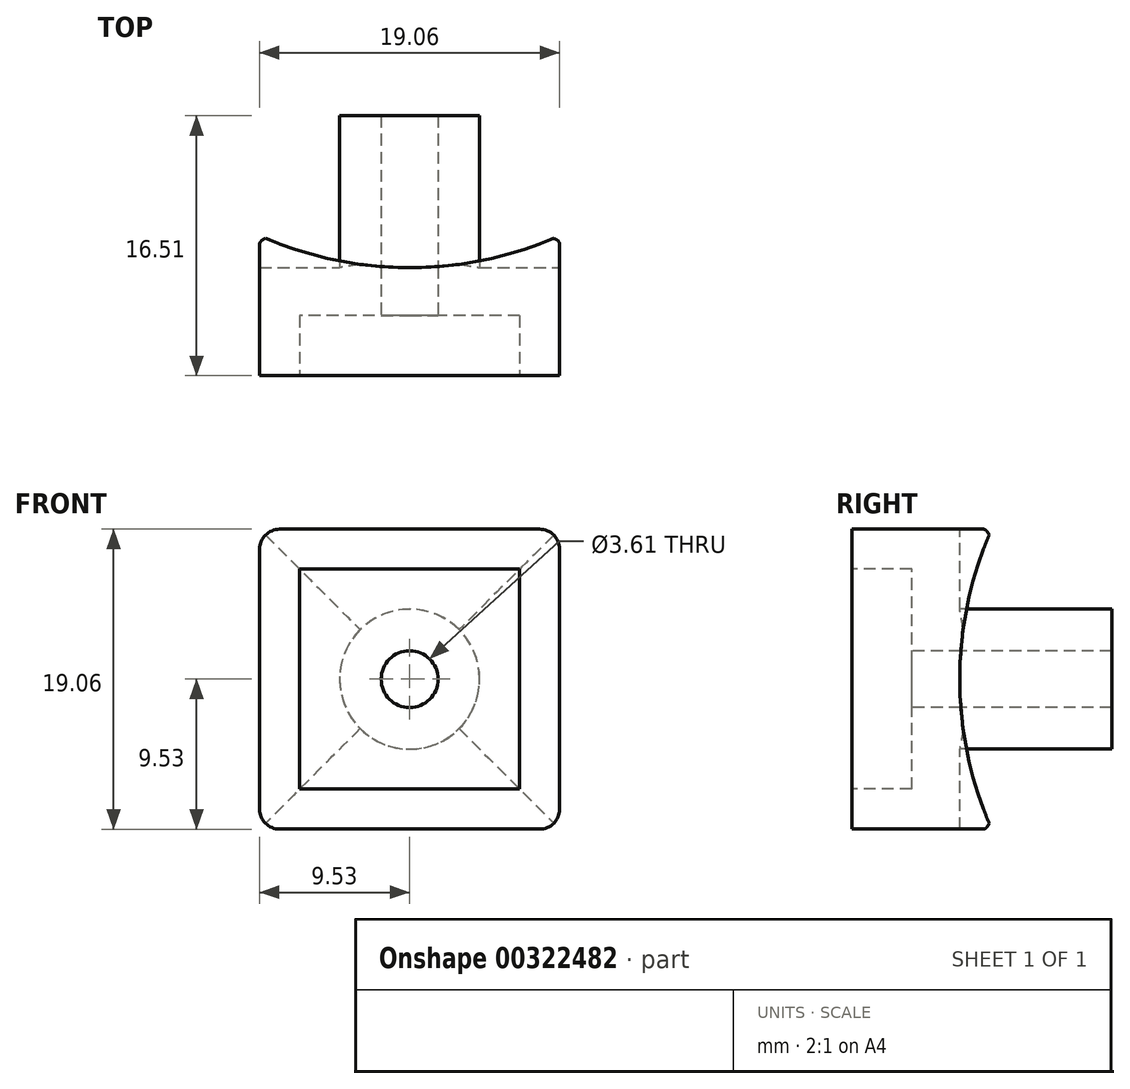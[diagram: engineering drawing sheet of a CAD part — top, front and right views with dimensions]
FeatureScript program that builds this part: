
annotation { "Feature Type Name" : "Feature", "Feature Type Description" : "" }
export const myFeature = defineFeature(function(context is Context, id is Id, definition is map)
    precondition{}
    {
        {
            var Q0;
            Q0=qCreatedBy(makeId("Front.planeOp"),FACE);
            var sketch = newSketch(context, id + "F0", { "sketchPlane" : qUnion([Q0])});
            skLineSegment(sketch, "E0.bottom", {"start": v(-9.52, -9.53) * mm, "end": v(9.53, -9.53) * mm});
            skLineSegment(sketch, "E0.top", {"start": v(-9.53, 9.53) * mm, "end": v(9.52, 9.53) * mm});
            skLineSegment(sketch, "E0.left", {"start": v(-9.52, -9.52) * mm, "end": v(-9.53, 9.52) * mm});
            skLineSegment(sketch, "E0.right", {"start": v(9.53, -9.52) * mm, "end": v(9.52, 9.53) * mm});
            skSolve(sketch);
        }
        {
            var Q0;
            Q0=makeQuery(id+"F0.imprint","IMPRINT",FACE,{"disambiguationData":[TD([[makeQuery(id+"F0.imprint","IMPRINT",EDGE,{"derivedFrom":sQuery(id+"F0.wireOp",EDGE,"E0.bottom")}),1.0]])]});
            extrude(context, id + "F1", {"entities" : qUnion([Q0]), "depth" : 11.43 * mm});
        }
        {
            var Q0;
            Q0=makeQuery(id+"F1.opExtrude","SWEPT_FACE",FACE,{"disambiguationData":[OSD([sQuery(id+"F0.wireOp",EDGE,"E0.right")])]});
            var sketch = newSketch(context, id + "F2", { "sketchPlane" : qUnion([Q0])});
            skArc(sketch, "E1", {"start": v(0, 9.52) * mm, "mid": v(-2.03, 0) * mm, "end": v(0, -9.52) * mm});
            skPoint(sketch, "E1.first.point", {"position": v(0, 9.52) * mm});
            skPoint(sketch, "E1.second.point", {"position": v(-2.03, 0) * mm});
            skPoint(sketch, "E1.third.point", {"position": v(0, -9.53) * mm});
            skLineSegment(sketch, "E2.0", {"start": v(-11.43, 9.52) * mm, "end": v(0, 9.52) * mm});
            skLineSegment(sketch, "E3.0", {"start": v(-11.43, -9.53) * mm, "end": v(0, -9.53) * mm});
            skSolve(sketch);
        }
        {
            var Q0;
            {var subQ1=sQuery(id+"F0.wireOp",EDGE,"E0.right");var subQ2=makeQuery(id+"F1.opExtrude","CAP_EDGE",EDGE,{"disambiguationData":[OSD([subQ1])],"isStart":true});Q0=makeQuery(id+"F2.imprint","IMPRINT",FACE,{"disambiguationData":[TD([[makeQuery(id+"F2.imprint","IMPRINT",EDGE,{"derivedFrom":subQ2}),1.0]])]});}
            extrude(context, id + "F3", {"entities" : qUnion([Q0]), "operationType" : NewBodyOperationType.REMOVE, "endBound" : BoundingType.THROUGH_ALL, "oppositeDirection" : true, "depth" : 25.4 * mm});
        }
        {
            var Q0;
            Q0=makeQuery(id+"F1.opExtrude","SWEPT_FACE",FACE,{"disambiguationData":[OSD([sQuery(id+"F0.wireOp",EDGE,"E0.top")])]});
            var sketch = newSketch(context, id + "F4", { "sketchPlane" : qUnion([Q0])});
            skCircle(sketch, "E4", {"center": v(0, 21.3) * mm, "radius": 23.34 * mm});
            skPoint(sketch, "E4.first.point", {"position": v(-9.53, 0) * mm});
            skPoint(sketch, "E4.second.point", {"position": v(0, -2.03) * mm});
            skPoint(sketch, "E4.third.point", {"position": v(9.52, 0) * mm});
            skSolve(sketch);
        }
        {
            var Q0;
            {var subQ1=sQuery(id+"F0.wireOp",EDGE,"E0.right");var subQ2=sQuery(id+"F0.wireOp",EDGE,"E0.top");var subQ3=makeQuery(id+"F3.boolean.opBoolean","MERGE",EDGE,{"derivedFrom":[makeQuery(id+"F1.opExtrude","CAP_EDGE",EDGE,{"disambiguationData":[OSD([subQ2])],"isStart":true}),makeQuery(id+"F3.opExtrude","SWEPT_EDGE",EDGE,{"disambiguationData":[OSD([subQ2,subQ1,sQuery(id+"F2.wireOp",EDGE,"E1")])]})]});Q0=makeQuery(id+"F4.imprint","IMPRINT",FACE,{"disambiguationData":[TD([[makeQuery(id+"F4.imprint","IMPRINT",EDGE,{"derivedFrom":subQ3}),-1.0]])]});}
            extrude(context, id + "F5", {"entities" : qUnion([Q0]), "operationType" : NewBodyOperationType.REMOVE, "endBound" : BoundingType.THROUGH_ALL, "oppositeDirection" : true, "depth" : 25.4 * mm});
        }
        {
            var Q0;
            Q0=makeQuery(id+"F1.opExtrude","CAP_FACE",FACE,{"disambiguationData":[OSD([sQuery(id+"F0.wireOp",EDGE,"E0.bottom"),sQuery(id+"F0.wireOp",EDGE,"E0.top"),sQuery(id+"F0.wireOp",EDGE,"E0.left"),sQuery(id+"F0.wireOp",EDGE,"E0.right")])],"isStart":false});
            var sketch = newSketch(context, id + "F6", { "sketchPlane" : qUnion([Q0])});
            skCircle(sketch, "E5", {"center": v(0, 0) * mm, "radius": 4.45 * mm});
            skCircle(sketch, "E6", {"center": v(0, 0) * mm, "radius": 1.8 * mm});
            skSolve(sketch);
        }
        {
            var Q0;
            Q0=makeQuery(id+"F6.imprint","IMPRINT",FACE,{"disambiguationData":[TD([[makeQuery(id+"F6.imprint","IMPRINT",EDGE,{"derivedFrom":sQuery(id+"F6.wireOp",EDGE,"E5")}),1.0]])]});
            extrude(context, id + "F7", {"entities" : qUnion([Q0]), "operationType" : NewBodyOperationType.ADD, "oppositeDirection" : true, "depth" : 19.05 * mm});
        }
        {
            var Q0;
            Q0=makeQuery(id+"F6.imprint","IMPRINT",FACE,{"disambiguationData":[TD([[makeQuery(id+"F6.imprint","IMPRINT",EDGE,{"derivedFrom":sQuery(id+"F6.wireOp",EDGE,"E6")}),1.0]])]});
            extrude(context, id + "F8", {"entities" : qUnion([Q0]), "operationType" : NewBodyOperationType.REMOVE, "endBound" : BoundingType.THROUGH_ALL, "oppositeDirection" : true, "depth" : 25.4 * mm});
        }
        {
            var Q0;
            Q0=makeQuery(id+"F1.opExtrude","SWEPT_FACE",FACE,{"disambiguationData":[OSD([sQuery(id+"F0.wireOp",EDGE,"E0.right")])]});
            var sketch = newSketch(context, id + "F9", { "sketchPlane" : qUnion([Q0])});
            skLineSegment(sketch, "E7.bottom", {"start": v(-11.43, -9.53) * mm, "end": v(-8.9, -9.53) * mm});
            skLineSegment(sketch, "E7.top", {"start": v(-11.43, 9.52) * mm, "end": v(-8.9, 9.52) * mm});
            skLineSegment(sketch, "E7.left", {"start": v(-11.43, -9.53) * mm, "end": v(-11.43, 9.52) * mm});
            skLineSegment(sketch, "E7.right", {"start": v(-8.9, -9.53) * mm, "end": v(-8.9, 9.52) * mm});
            skSolve(sketch);
        }
        {
            var Q0;
            Q0=makeQuery(id+"F9.imprint","IMPRINT",FACE,{"disambiguationData":[TD([[makeQuery(id+"F9.imprint","IMPRINT",EDGE,{"derivedFrom":sQuery(id+"F9.wireOp",EDGE,"E7.bottom")}),1.0]])]});
            extrude(context, id + "F10", {"entities" : qUnion([Q0]), "operationType" : NewBodyOperationType.REMOVE, "endBound" : BoundingType.THROUGH_ALL, "oppositeDirection" : true, "depth" : 25.4 * mm});
        }
        {
            var Q0;
            Q0=makeQuery(id+"F6.imprint","IMPRINT",FACE,{"disambiguationData":[TD([[makeQuery(id+"F6.imprint","IMPRINT",EDGE,{"derivedFrom":sQuery(id+"F6.wireOp",EDGE,"E5")}),-1.0]])]});
            var sketch = newSketch(context, id + "F11", { "sketchPlane" : qUnion([Q0])});
            skLineSegment(sketch, "E8.bottom", {"start": v(6.99, -6.98) * mm, "end": v(-6.98, -6.99) * mm});
            skLineSegment(sketch, "E8.top", {"start": v(6.98, 6.98) * mm, "end": v(-6.99, 6.98) * mm});
            skLineSegment(sketch, "E8.left", {"start": v(6.99, -6.98) * mm, "end": v(6.98, 6.98) * mm});
            skLineSegment(sketch, "E8.right", {"start": v(-6.98, -6.99) * mm, "end": v(-6.99, 6.98) * mm});
            skSolve(sketch);
        }
        {
            var Q0;
            Q0=makeQuery(id+"F11.imprint","IMPRINT",FACE,{"disambiguationData":[TD([[makeQuery(id+"F11.imprint","IMPRINT",EDGE,{"derivedFrom":sQuery(id+"F11.wireOp",EDGE,"E8.bottom")}),-1.0]])]});
            var Q1;
            Q1=makeQuery(id+"F6.imprint","IMPRINT",FACE,{"disambiguationData":[TD([[makeQuery(id+"F6.imprint","IMPRINT",EDGE,{"derivedFrom":sQuery(id+"F6.wireOp",EDGE,"E5")}),1.0]])]});
            extrude(context, id + "F12", {"entities" : qUnion([Q0, Q1]), "operationType" : NewBodyOperationType.REMOVE, "oppositeDirection" : true, "depth" : 6.35 * mm});
        }
        {
            var Q0;
            Q0=makeQuery(id+"F1.opExtrude","SWEPT_EDGE",EDGE,{"disambiguationData":[OSD([sQuery(id+"F0.wireOp",EDGE,"E0.bottom"),sQuery(id+"F0.wireOp",EDGE,"E0.left")])]});
            var Q1;
            Q1=makeQuery(id+"F1.opExtrude","SWEPT_EDGE",EDGE,{"disambiguationData":[OSD([sQuery(id+"F0.wireOp",EDGE,"E0.top"),sQuery(id+"F0.wireOp",EDGE,"E0.left")])]});
            var Q2;
            Q2=makeQuery(id+"F1.opExtrude","SWEPT_EDGE",EDGE,{"disambiguationData":[OSD([sQuery(id+"F0.wireOp",EDGE,"E0.top"),sQuery(id+"F0.wireOp",EDGE,"E0.right")])]});
            var Q3;
            Q3=makeQuery(id+"F1.opExtrude","SWEPT_EDGE",EDGE,{"disambiguationData":[OSD([sQuery(id+"F0.wireOp",EDGE,"E0.bottom"),sQuery(id+"F0.wireOp",EDGE,"E0.right")])]});
            fillet(context, id + "F13", {"entities" : qUnion([Q0, Q1, Q2, Q3]), "radius" : 1.27 * mm, "tangentPropagation" : true, "allowEdgeOverflow" : false});
        }
    });
